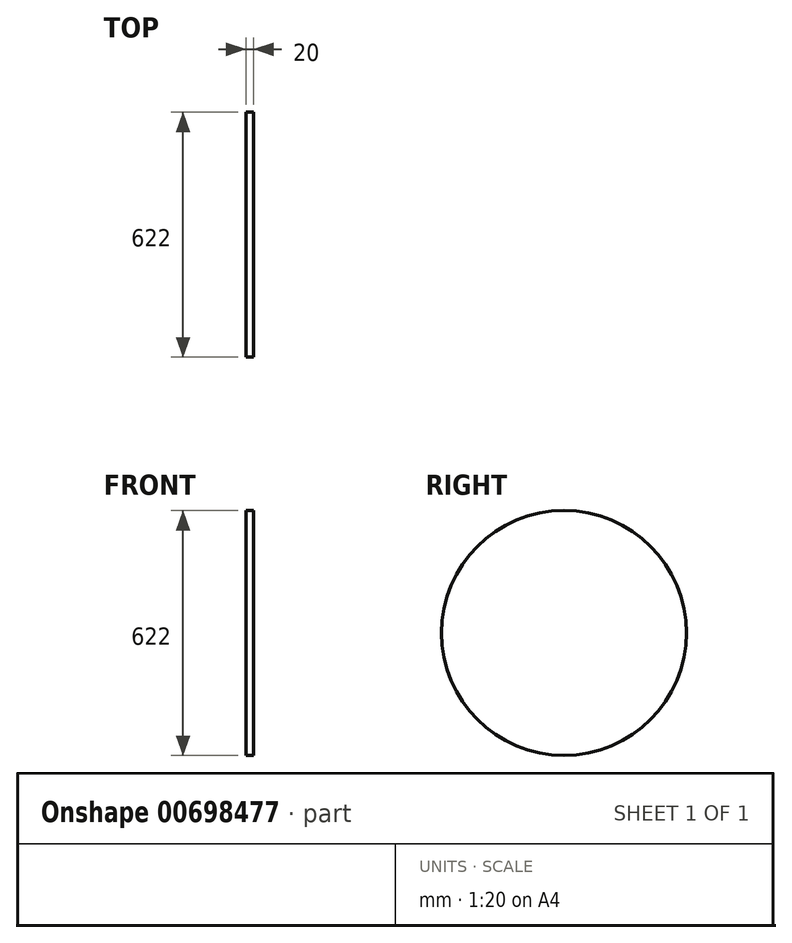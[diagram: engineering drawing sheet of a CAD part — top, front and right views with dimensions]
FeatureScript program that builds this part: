
annotation { "Feature Type Name" : "Feature", "Feature Type Description" : "" }
export const myFeature = defineFeature(function(context is Context, id is Id, definition is map)
    precondition{}
    {
        {
            var Q0;
            Q0=qCreatedBy(makeId("Front.planeOp"),FACE);
            var sketch = newSketch(context, id + "F0", { "sketchPlane" : qUnion([Q0])});
            skLineSegment(sketch, "E0.bottom", {"start": v(-7.5, 311) * mm, "end": v(12.5, 311) * mm});
            skLineSegment(sketch, "E0.top", {"start": v(-7.5, 0) * mm, "end": v(12.5, 0) * mm});
            skLineSegment(sketch, "E0.left", {"start": v(-7.5, 311) * mm, "end": v(-7.5, 0) * mm});
            skLineSegment(sketch, "E0.right", {"start": v(12.5, 311) * mm, "end": v(12.5, 0) * mm});
            skSolve(sketch);
        }
        {
            var Q0;
            Q0=makeQuery(id+"F0.imprint","IMPRINT",FACE,{"disambiguationData":[TD([[makeQuery(id+"F0.imprint","IMPRINT",EDGE,{"derivedFrom":sQuery(id+"F0.wireOp",EDGE,"E0.bottom")}),-1.0]])]});
            var Q1;
            Q1=sQuery(id+"F0.wireOp",EDGE,"E0.top");
            revolve(context, id + "F1", {"entities" : qUnion([Q0]), "axis" : qUnion([Q1]), "revolveType" : RevolveType.FULL});
        }
    });
